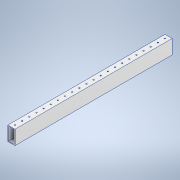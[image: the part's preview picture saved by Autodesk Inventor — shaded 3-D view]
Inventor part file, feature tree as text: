
AUTODESK INVENTOR PART (.ipt)
format: ipt  version: 2020 (Build 240168000, 168)  size: 151,040 bytes
history: native  units: in
note: dims shown in document units (in); Inventor stores cm internally (conversion verified against a paired STEP export)
features: sketch x2, extrude x1, hole x1
ambient origin geometry x8: Origin, YZ Plane, XZ Plane, XY Plane, X Axis, Y Axis, Z Axis, Center Point
bodies: Solid1 (feature_tree)
feature tree (4):
  extrude  "Extrusion1"  Depth=2.0in
  hole  "Hole1"  [1 undecoded]
  sketch  "Sketch1"  dims[d0=1.0in d1=2.0in]
  sketch  "Sketch2"  dims[d2=0.1in d3=22.0in d4=0.0in d5=0.5in d6=0.5in d7=9.4488in d9=1.0in d10=0.3937in d12=1.0in d14=0.163in d15=0.75in d16=0.375in d17=0.25in d18=0.5635in d19=1.0in d20=0.8108in]
note: 1 required parameter value undecoded (feature->parameter linkage not recoverable at this tier; creation-order binding heuristic only, values carry confidence <= 0.55)
